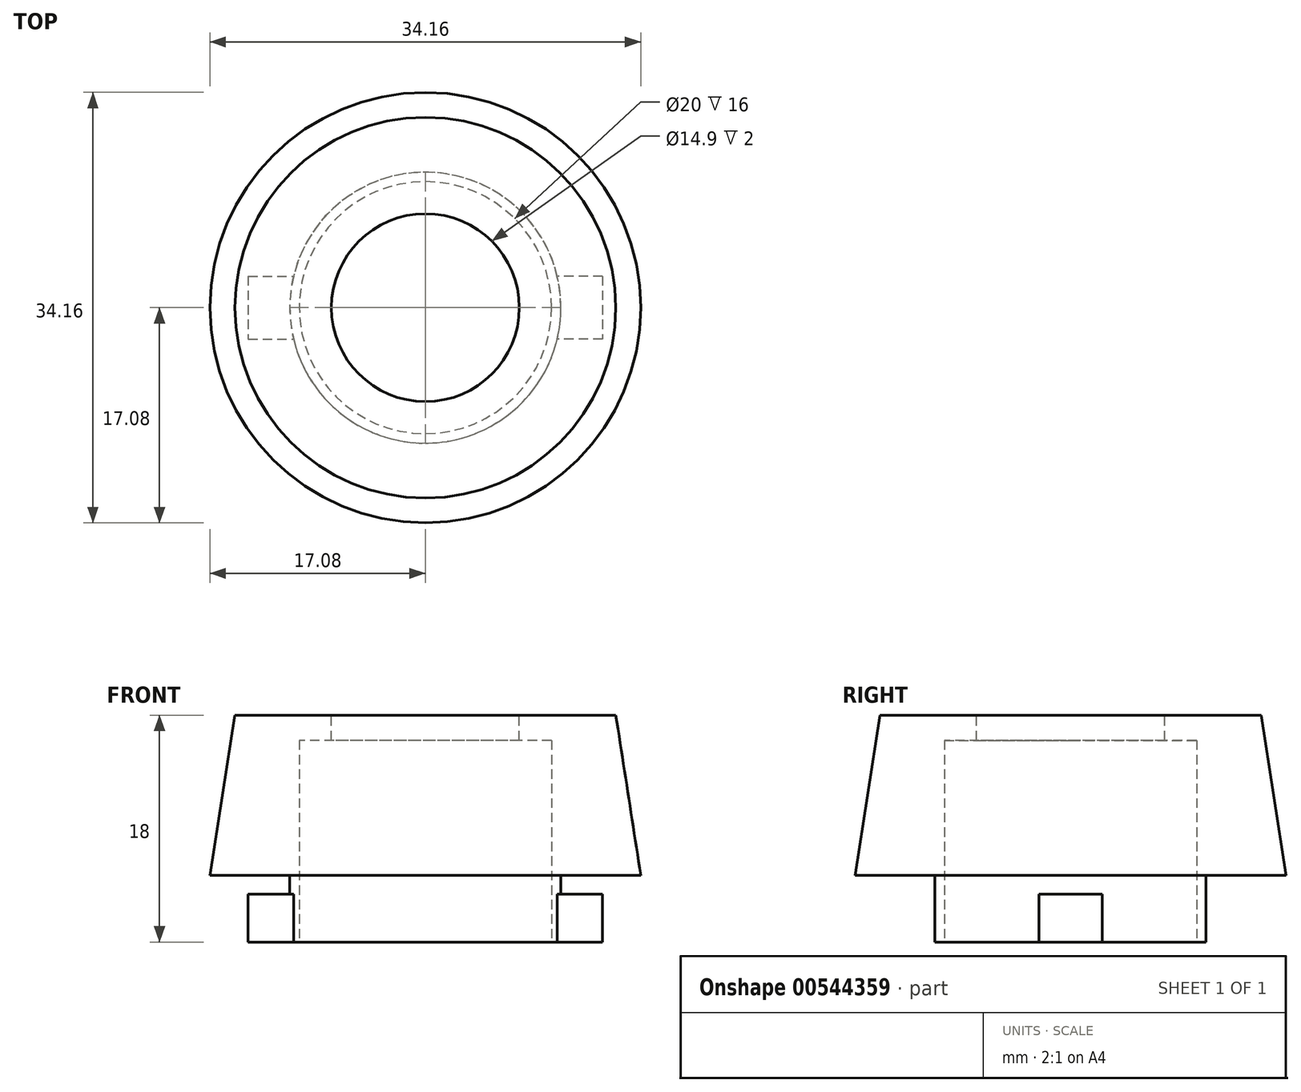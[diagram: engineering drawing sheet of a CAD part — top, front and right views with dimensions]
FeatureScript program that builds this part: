
annotation { "Feature Type Name" : "Feature", "Feature Type Description" : "" }
export const myFeature = defineFeature(function(context is Context, id is Id, definition is map)
    precondition{}
    {
        {
            var Q0;
            Q0=qCreatedBy(makeId("Top.planeOp"),FACE);
            var sketch = newSketch(context, id + "F0", { "sketchPlane" : qUnion([Q0])});
            skCircle(sketch, "E0", {"center": v(0, 0) * mm, "radius": 15.1 * mm});
            skSolve(sketch);
        }
        {
            var Q0;
            Q0=qCreatedBy(makeId("Top.planeOp"),FACE);
            cPlane(context, id + "F1", {"entities" : qUnion([Q0]), "cplaneType" : CPlaneType.OFFSET, "offset" : 12.7 * mm, "oppositeDirection" : true, "width" : 150 * mm, "height" : 150 * mm});
        }
        {
            var Q0;
            Q0=qCreatedBy(id+"F1.planeOp",FACE);
            var sketch = newSketch(context, id + "F2", { "sketchPlane" : qUnion([Q0])});
            skCircle(sketch, "E1", {"center": v(0, 0) * mm, "radius": 17.07 * mm});
            skSolve(sketch);
        }
        {
            var Q0;
            Q0=makeQuery(id+"F2.imprint","IMPRINT",FACE,{"disambiguationData":[TD([[makeQuery(id+"F2.imprint","IMPRINT",EDGE,{"derivedFrom":sQuery(id+"F2.wireOp",EDGE,"E1")}),1.0]])]});
            var Q1;
            Q1=makeQuery(id+"F0.imprint","IMPRINT",FACE,{"disambiguationData":[TD([[makeQuery(id+"F0.imprint","IMPRINT",EDGE,{"derivedFrom":sQuery(id+"F0.wireOp",EDGE,"E0")}),1.0]])]});
            loft(context, id + "F3", {"sheetProfilesArray" : [{ "sheetProfileEntities" : qUnion([Q0]) }, { "sheetProfileEntities" : qUnion([Q1]) }]});
        }
        {
            var Q0;
            Q0=qCreatedBy(makeId("Top.planeOp"),FACE);
            cPlane(context, id + "F4", {"entities" : qUnion([Q0]), "cplaneType" : CPlaneType.OFFSET, "offset" : 18 * mm, "oppositeDirection" : true, "width" : 150 * mm, "height" : 150 * mm});
        }
        {
            var Q0;
            Q0=qCreatedBy(id+"F4.planeOp",FACE);
            var sketch = newSketch(context, id + "F5", { "sketchPlane" : qUnion([Q0])});
            skCircle(sketch, "E2", {"center": v(0, 0) * mm, "radius": 10.75 * mm});
            skCircle(sketch, "E3", {"center": v(0, 0) * mm, "radius": 10 * mm});
            skSolve(sketch);
        }
        {
            var Q0;
            Q0=makeQuery(id+"F5.imprint","IMPRINT",FACE,{"disambiguationData":[TD([[makeQuery(id+"F5.imprint","IMPRINT",EDGE,{"derivedFrom":sQuery(id+"F5.wireOp",EDGE,"E2")}),1.0]])]});
            extrude(context, id + "F6", {"entities" : qUnion([Q0]), "operationType" : NewBodyOperationType.ADD, "depth" : 18 * mm, "offsetDistance" : 25 * mm});
        }
        {
            var Q0;
            Q0=makeQuery(id+"F6.boolean.opBoolean","SPLIT",FACE,{"disambiguationData":[TD([makeQuery(id+"F6.opExtrude","SWEPT_FACE",FACE,{"disambiguationData":[OSD([sQuery(id+"F5.wireOp",EDGE,"E3")])]})])],"derivedFrom":makeQuery(id+"F3.opLoft","CAP_FACE",FACE,{"disambiguationData":[OSD([makeQuery(id+"F2.imprint","IMPRINT",FACE,{"disambiguationData":[TD([[makeQuery(id+"F2.imprint","IMPRINT",EDGE,{"derivedFrom":sQuery(id+"F2.wireOp",EDGE,"E1")}),1.0]])]})])],"isStart":true})});
            extrude(context, id + "F7", {"entities" : qUnion([Q0]), "operationType" : NewBodyOperationType.REMOVE, "oppositeDirection" : true, "depth" : 18 * mm, "offsetDistance" : 25 * mm});
        }
        {
            var Q0;
            Q0=qCreatedBy(makeId("Top.planeOp"),FACE);
            var sketch = newSketch(context, id + "F8", { "sketchPlane" : qUnion([Q0])});
            skCircle(sketch, "E4", {"center": v(0, 0) * mm, "radius": 7.45 * mm});
            skCircle(sketch, "E5.0", {"center": v(0, 0) * mm, "radius": 10 * mm});
            skSolve(sketch);
        }
        {
            var Q0;
            Q0=makeQuery(id+"F8.imprint","IMPRINT",FACE,{"disambiguationData":[TD([[makeQuery(id+"F8.imprint","IMPRINT",EDGE,{"derivedFrom":sQuery(id+"F8.wireOp",EDGE,"E4")}),-1.0]])]});
            extrude(context, id + "F9", {"entities" : qUnion([Q0]), "operationType" : NewBodyOperationType.ADD, "oppositeDirection" : true, "depth" : 2 * mm, "offsetDistance" : 25 * mm});
        }
        {
            var Q0;
            Q0=makeQuery(id+"F6.opExtrude","CAP_FACE",FACE,{"disambiguationData":[OSD([sQuery(id+"F5.wireOp",EDGE,"E2"),sQuery(id+"F5.wireOp",EDGE,"E3")])],"isStart":true});
            var sketch = newSketch(context, id + "F10", { "sketchPlane" : qUnion([Q0])});
            skLineSegment(sketch, "E6", {"start": v(-14.05, 0) * mm, "end": v(-14.05, 2.5) * mm});
            skLineSegment(sketch, "E7", {"start": v(-14.05, 2.5) * mm, "end": v(-10.46, 2.5) * mm});
            skLineSegment(sketch, "E8.MirrorCS", {"start": v(-14.05, -2.5) * mm, "end": v(-10.46, -2.5) * mm});
            skLineSegment(sketch, "E9.MirrorCS", {"start": v(-14.05, 0) * mm, "end": v(-14.05, -2.5) * mm});
            skLineSegment(sketch, "E10.MirrorCS", {"start": v(14.05, 2.5) * mm, "end": v(10.46, 2.5) * mm});
            skLineSegment(sketch, "E11.MirrorCS", {"start": v(14.05, 0) * mm, "end": v(14.05, 2.5) * mm});
            skLineSegment(sketch, "E12.MirrorCS", {"start": v(14.05, 0) * mm, "end": v(14.05, -2.5) * mm});
            skLineSegment(sketch, "E13.MirrorCS", {"start": v(14.05, -2.5) * mm, "end": v(10.46, -2.5) * mm});
            skSolve(sketch);
        }
        {
            var Q0;
            Q0=makeQuery(id+"F10.imprint","IMPRINT",FACE,{"disambiguationData":[TD([[makeQuery(id+"F10.imprint","IMPRINT",EDGE,{"derivedFrom":sQuery(id+"F10.wireOp",EDGE,"E6")}),-1.0]])]});
            var Q1;
            {var subQ1=sQuery(id+"F10.wireOp",EDGE,"E10.MirrorCS");Q1=makeQuery(id+"F10.imprint","IMPRINT",FACE,{"disambiguationData":[TD([[makeQuery(id+"F10.imprint","IMPRINT",EDGE,{"derivedFrom":subQ1}),1.0]])]});}
            extrude(context, id + "F11", {"entities" : qUnion([Q0, Q1]), "operationType" : NewBodyOperationType.ADD, "oppositeDirection" : true, "depth" : 3.8 * mm, "offsetDistance" : 25 * mm});
        }
    });
